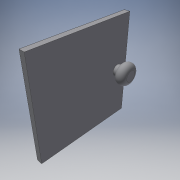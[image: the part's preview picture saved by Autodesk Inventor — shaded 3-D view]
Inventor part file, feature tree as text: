
AUTODESK INVENTOR PART (.ipt)
format: ipt  version: 2016 (Build 200138000, 138)  size: 114,176 bytes
history: native  units: in
note: dims shown in document units (in); Inventor stores cm internally (conversion verified against a paired STEP export)
features: extrude x3, sketch x3, fillet x1
ambient origin geometry x8: Origin, YZ Plane, XZ Plane, XY Plane, X Axis, Y Axis, Z Axis, Center Point
bodies: Solid1 (feature_tree)
feature tree (7):
  extrude  "Extrusion1"  Depth=18.0in
  extrude  "Extrusion2"  Depth=1.0in
  extrude  "Extrusion3"  Depth=1.0in TaperAngle=0.0deg
  fillet  "Fillet1"  Radius=2.0in
  sketch  "Sketch1"  dims[d0=18.0in d1=18.0in]
  sketch  "Sketch2"  dims[d2=1.0in d3=0.0in d4=2.0in]
  sketch  "Sketch3"  dims[d5=2.0in d6=0.75in d7=0.0in d8=2.0in d9=4.0in d10=2.0in d11=0.0in d12=1.0in]
